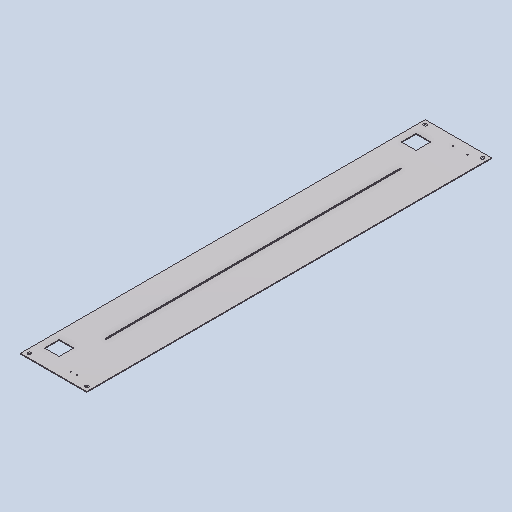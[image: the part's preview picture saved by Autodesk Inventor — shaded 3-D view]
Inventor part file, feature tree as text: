
AUTODESK INVENTOR PART (.ipt)
format: ipt  version: 2025 (Build 290162010, 162A)  size: 223,744 bytes
history: native  units: mm
features: sketch x3, extrude x2, hole x1, other x1
ambient origin geometry x8: Origin, YZ Plane, XZ Plane, XY Plane, X Axis, Y Axis, Z Axis, Center Point
bodies: Volumenkörper1 (feature_tree)
feature tree (7):
  extrude  "Extrusion1"  Depth=40.0mm
  extrude  "Extrusion2"  Depth=525.0mm
  hole  "Bohrung1"  [1 undecoded]
  sketch  "Skizze1"  dims[d0=3.0mm d1=40.0mm]
  sketch  "Skizze2"  dims[d2=40.249122mm d3=525.0mm]
  sketch  "Skizze3"  dims[d4=0.0mm d5=0.0mm d6=16.712001mm d8=51.636694mm d9=525.0mm d10=4.0mm d14=98.05mm d15=800.0mm d16=20.0mm d17=40.0mm d18=45.0mm d19=1.0mm d20=0.0mm d21=0.0mm d22=12.0mm d23=4.3mm d24=5.0mm d25=9.4mm d26=2.0mm d27=15.7mm d28=6.3mm d29=20.594885mm d7=0.15mm d11=0.75mm d12=1180.0mm d13=0.0625mm]
  other  "item_0047308_Blech Al 2mm_L=1100_B=180_1"
note: 1 required parameter value undecoded (feature->parameter linkage not recoverable at this tier; creation-order binding heuristic only, values carry confidence <= 0.55)
